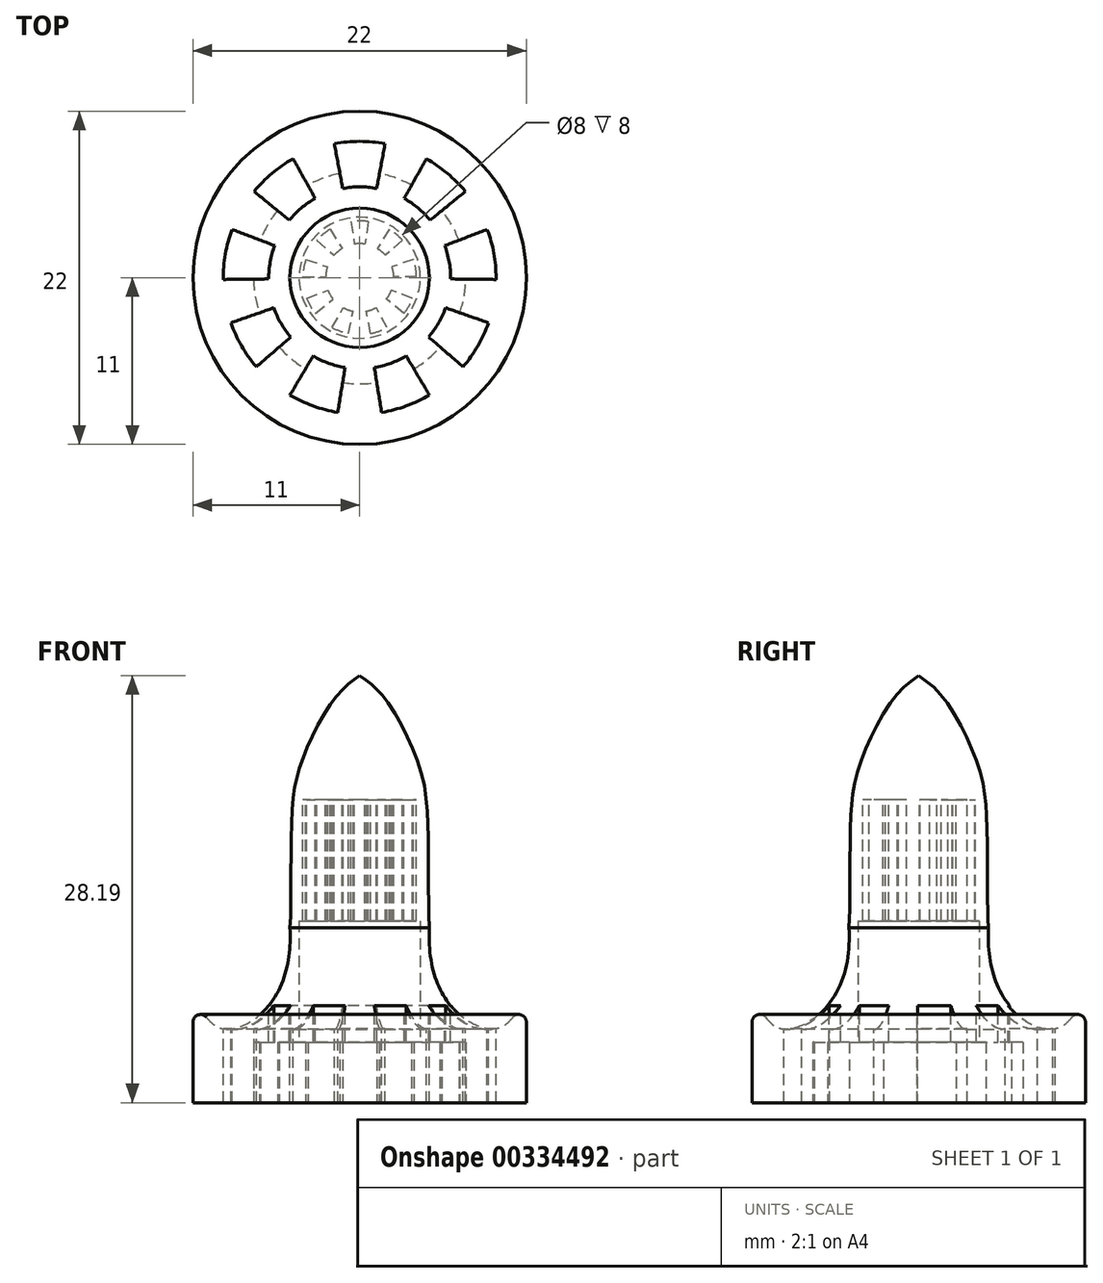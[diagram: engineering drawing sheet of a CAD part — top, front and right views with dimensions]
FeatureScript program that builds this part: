
annotation { "Feature Type Name" : "Feature", "Feature Type Description" : "" }
export const myFeature = defineFeature(function(context is Context, id is Id, definition is map)
    precondition{}
    {
        {
            var Q0;
            Q0=qCreatedBy(makeId("Top.planeOp"),FACE);
            var sketch = newSketch(context, id + "F0", { "sketchPlane" : qUnion([Q0])});
            skCircle(sketch, "E0", {"center": v(0, 0) * mm, "radius": 11 * mm});
            skSolve(sketch);
        }
        {
            var Q0;
            Q0=qSketchRegion(id+"F0",true);
            extrude(context, id + "F1", {"entities" : qUnion([Q0]), "depth" : 2 * mm});
        }
        {
            var Q0;
            Q0=qCreatedBy(makeId("Front.planeOp"),FACE);
            var sketch = newSketch(context, id + "F2", { "sketchPlane" : qUnion([Q0])});
            skPoint(sketch, "E1", {"position": v(0, 21.19) * mm});
            skLineSegment(sketch, "E2", {"start": v(0, 21.19) * mm, "end": v(0, 2) * mm});
            skLineSegment(sketch, "E3", {"start": v(-11, 2) * mm, "end": v(0, 2) * mm});
            skLineSegment(sketch, "E4", {"start": v(-11, 2) * mm, "end": v(-11, 7.23) * mm});
            skFitSpline(sketch, "E5", {"points": [v(-11, 7.23) * mm, v(-9.2, 4.92) * mm, v(-6.25, 6.13) * mm, v(-4.6, 11.53) * mm], "startDerivative": vector(4.68, -10.12) * mm, "endDerivative": vector(-0.82, 17.56) * mm});
            skLineSegment(sketch, "E6", {"start": v(0, 21.19) * mm, "end": v(0, 28.19) * mm});
            skFitSpline(sketch, "E7", {"points": [v(0, 28.19) * mm, v(-1.53, 26.84) * mm, v(-3.73, 22.78) * mm, v(-4.47, 18.95) * mm, v(-4.6, 11.53) * mm], "startDerivative": vector(-7.87, -5.55) * mm, "endDerivative": vector(-1, -14.63) * mm});
            skSolve(sketch);
        }
        {
            var Q0;
            Q0=qSketchRegion(id+"F2",true);
            var Q1;
            Q1=sQuery(id+"F2.wireOp",EDGE,"E2");
            revolve(context, id + "F3", {"operationType" : NewBodyOperationType.ADD, "entities" : qUnion([Q0]), "axis" : qUnion([Q1]), "revolveType" : RevolveType.FULL});
        }
        {
            var Q0;
            Q0=makeQuery(id+"F1.opExtrude","CAP_FACE",FACE,{"disambiguationData":[OSD([sQuery(id+"F0.wireOp",EDGE,"E0")])],"isStart":true});
            var sketch = newSketch(context, id + "F4", { "sketchPlane" : qUnion([Q0])});
            skCircle(sketch, "E8", {"center": v(0, 0) * mm, "radius": 7 * mm});
            skSolve(sketch);
        }
        {
            var Q0;
            Q0=qSketchRegion(id+"F4",true);
            extrude(context, id + "F5", {"entities" : qUnion([Q0]), "operationType" : NewBodyOperationType.REMOVE, "oppositeDirection" : true, "depth" : 4 * mm});
        }
        {
            var Q0;
            Q0=makeQuery(id+"F5.boolean.opBoolean","COPY",FACE,{"derivedFrom":makeQuery(id+"F5.opExtrude","CAP_FACE",FACE,{"disambiguationData":[OSD([sQuery(id+"F4.wireOp",EDGE,"E8")])],"isStart":false})});
            var sketch = newSketch(context, id + "F6", { "sketchPlane" : qUnion([Q0])});
            skCircle(sketch, "E9", {"center": v(0, 0) * mm, "radius": 4 * mm});
            skSolve(sketch);
        }
        {
            var Q0;
            Q0=qSketchRegion(id+"F6",true);
            extrude(context, id + "F7", {"entities" : qUnion([Q0]), "operationType" : NewBodyOperationType.REMOVE, "oppositeDirection" : true, "depth" : 8 * mm});
        }
        {
            var Q0;
            Q0=qCreatedBy(makeId("Top.planeOp"),FACE);
            cPlane(context, id + "F8", {"entities" : qUnion([Q0]), "cplaneType" : CPlaneType.OFFSET, "offset" : 20 * mm, "width" : 150 * mm, "height" : 150 * mm});
        }
        {
            var Q0;
            Q0=qCreatedBy(id+"F8.planeOp",FACE);
            var sketch = newSketch(context, id + "F9", { "sketchPlane" : qUnion([Q0])});
            skArc(sketch, "E10", {"start": v(1.12, 5.9) * mm, "mid": v(0, 6) * mm, "end": v(-1.12, 5.9) * mm});
            skArc(sketch, "E11", {"start": v(1.68, 8.84) * mm, "mid": v(0, 9) * mm, "end": v(-1.68, 8.84) * mm});
            skLineSegment(sketch, "E12", {"start": v(1.12, 5.9) * mm, "end": v(1.68, 8.84) * mm});
            skLineSegment(sketch, "E13.MirrorCS", {"start": v(-1.12, 5.9) * mm, "end": v(-1.68, 8.84) * mm});
            skLineSegment(sketch, "E14.1.0", {"start": v(-2.93, 5.23) * mm, "end": v(-4.4, 7.85) * mm});
            skArc(sketch, "E14.1.1", {"start": v(-4.4, 7.85) * mm, "mid": v(-5.79, 6.9) * mm, "end": v(-6.97, 5.7) * mm});
            skLineSegment(sketch, "E14.1.2", {"start": v(-4.65, 3.8) * mm, "end": v(-6.97, 5.7) * mm});
            skArc(sketch, "E14.1.3", {"start": v(-2.93, 5.23) * mm, "mid": v(-3.86, 4.6) * mm, "end": v(-4.65, 3.8) * mm});
            skLineSegment(sketch, "E14.2.0", {"start": v(-5.61, 2.12) * mm, "end": v(-8.42, 3.19) * mm});
            skArc(sketch, "E14.2.1", {"start": v(-8.42, 3.19) * mm, "mid": v(-8.86, 1.56) * mm, "end": v(-9, -0.11) * mm});
            skLineSegment(sketch, "E14.2.2", {"start": v(-6, -0.08) * mm, "end": v(-9, -0.11) * mm});
            skArc(sketch, "E14.2.3", {"start": v(-5.61, 2.12) * mm, "mid": v(-5.9, 1.04) * mm, "end": v(-6, -0.08) * mm});
            skLineSegment(sketch, "E14.3.0", {"start": v(-5.66, -1.98) * mm, "end": v(-8.5, -2.97) * mm});
            skArc(sketch, "E14.3.1", {"start": v(-8.5, -2.97) * mm, "mid": v(-7.8, -4.5) * mm, "end": v(-6.82, -5.87) * mm});
            skLineSegment(sketch, "E14.3.2", {"start": v(-4.55, -3.92) * mm, "end": v(-6.82, -5.87) * mm});
            skArc(sketch, "E14.3.3", {"start": v(-5.66, -1.98) * mm, "mid": v(-5.2, -3) * mm, "end": v(-4.55, -3.92) * mm});
            skLineSegment(sketch, "E14.4.0", {"start": v(-3.07, -5.16) * mm, "end": v(-4.6, -7.74) * mm});
            skArc(sketch, "E14.4.1", {"start": v(-4.6, -7.74) * mm, "mid": v(-3.08, -8.46) * mm, "end": v(-1.45, -8.88) * mm});
            skLineSegment(sketch, "E14.4.2", {"start": v(-0.97, -5.92) * mm, "end": v(-1.45, -8.88) * mm});
            skArc(sketch, "E14.4.3", {"start": v(-3.07, -5.16) * mm, "mid": v(-2.05, -5.64) * mm, "end": v(-0.97, -5.92) * mm});
            skLineSegment(sketch, "E14.5.0", {"start": v(0.97, -5.92) * mm, "end": v(1.45, -8.88) * mm});
            skArc(sketch, "E14.5.1", {"start": v(1.45, -8.88) * mm, "mid": v(3.08, -8.46) * mm, "end": v(4.6, -7.74) * mm});
            skLineSegment(sketch, "E14.5.2", {"start": v(3.07, -5.16) * mm, "end": v(4.6, -7.74) * mm});
            skArc(sketch, "E14.5.3", {"start": v(0.97, -5.92) * mm, "mid": v(2.05, -5.64) * mm, "end": v(3.07, -5.16) * mm});
            skLineSegment(sketch, "E14.6.0", {"start": v(4.55, -3.92) * mm, "end": v(6.82, -5.87) * mm});
            skArc(sketch, "E14.6.1", {"start": v(6.82, -5.87) * mm, "mid": v(7.8, -4.5) * mm, "end": v(8.5, -2.97) * mm});
            skLineSegment(sketch, "E14.6.2", {"start": v(5.66, -1.98) * mm, "end": v(8.5, -2.97) * mm});
            skArc(sketch, "E14.6.3", {"start": v(4.55, -3.92) * mm, "mid": v(5.2, -3) * mm, "end": v(5.66, -1.98) * mm});
            skLineSegment(sketch, "E14.7.0", {"start": v(6, -0.08) * mm, "end": v(9, -0.11) * mm});
            skArc(sketch, "E14.7.1", {"start": v(9, -0.11) * mm, "mid": v(8.86, 1.56) * mm, "end": v(8.42, 3.19) * mm});
            skLineSegment(sketch, "E14.7.2", {"start": v(5.61, 2.12) * mm, "end": v(8.42, 3.19) * mm});
            skArc(sketch, "E14.7.3", {"start": v(6, -0.08) * mm, "mid": v(5.9, 1.04) * mm, "end": v(5.61, 2.12) * mm});
            skLineSegment(sketch, "E14.8.0", {"start": v(4.65, 3.8) * mm, "end": v(6.97, 5.7) * mm});
            skArc(sketch, "E14.8.1", {"start": v(6.97, 5.7) * mm, "mid": v(5.79, 6.9) * mm, "end": v(4.4, 7.85) * mm});
            skLineSegment(sketch, "E14.8.2", {"start": v(2.93, 5.23) * mm, "end": v(4.4, 7.85) * mm});
            skArc(sketch, "E14.8.3", {"start": v(4.65, 3.8) * mm, "mid": v(3.86, 4.6) * mm, "end": v(2.93, 5.23) * mm});
            skSolve(sketch);
        }
        {
            var Q0;
            Q0=qSketchRegion(id+"F9",true);
            extrude(context, id + "F10", {"entities" : qUnion([Q0]), "operationType" : NewBodyOperationType.REMOVE, "oppositeDirection" : true, "depth" : 25 * mm});
        }
        {
            var Q0;
            Q0=qCreatedBy(id+"F8.planeOp",FACE);
            var sketch = newSketch(context, id + "F11", { "sketchPlane" : qUnion([Q0])});
            skArc(sketch, "E15", {"start": v(0.34, 2.22) * mm, "mid": v(0, 2.25) * mm, "end": v(-0.34, 2.22) * mm});
            skArc(sketch, "E16", {"start": v(0.57, 3.7) * mm, "mid": v(0, 3.75) * mm, "end": v(-0.57, 3.7) * mm});
            skLineSegment(sketch, "E17", {"start": v(0.34, 2.22) * mm, "end": v(0.57, 3.7) * mm});
            skLineSegment(sketch, "E18.MirrorCS", {"start": v(-0.34, 2.22) * mm, "end": v(-0.57, 3.7) * mm});
            skLineSegment(sketch, "E19.1.0", {"start": v(-1.7, 1.48) * mm, "end": v(-2.82, 2.47) * mm});
            skArc(sketch, "E19.1.1", {"start": v(-1.94, 3.2) * mm, "mid": v(-2.41, 2.87) * mm, "end": v(-2.82, 2.47) * mm});
            skLineSegment(sketch, "E19.1.2", {"start": v(-1.17, 1.92) * mm, "end": v(-1.94, 3.2) * mm});
            skArc(sketch, "E19.1.3", {"start": v(-1.17, 1.92) * mm, "mid": v(-1.45, 1.72) * mm, "end": v(-1.7, 1.48) * mm});
            skLineSegment(sketch, "E19.2.0", {"start": v(-2.25, 0.05) * mm, "end": v(-3.75, 0.08) * mm});
            skArc(sketch, "E19.2.1", {"start": v(-3.55, 1.2) * mm, "mid": v(-3.7, 0.65) * mm, "end": v(-3.75, 0.08) * mm});
            skLineSegment(sketch, "E19.2.2", {"start": v(-2.13, 0.73) * mm, "end": v(-3.55, 1.2) * mm});
            skArc(sketch, "E19.2.3", {"start": v(-2.13, 0.73) * mm, "mid": v(-2.22, 0.4) * mm, "end": v(-2.25, 0.05) * mm});
            skLineSegment(sketch, "E19.3.0", {"start": v(-1.75, -1.41) * mm, "end": v(-2.92, -2.35) * mm});
            skArc(sketch, "E19.3.1", {"start": v(-3.5, -1.36) * mm, "mid": v(-3.25, -1.87) * mm, "end": v(-2.92, -2.35) * mm});
            skLineSegment(sketch, "E19.3.2", {"start": v(-2.1, -0.81) * mm, "end": v(-3.5, -1.36) * mm});
            skArc(sketch, "E19.3.3", {"start": v(-2.1, -0.81) * mm, "mid": v(-1.95, -1.12) * mm, "end": v(-1.75, -1.41) * mm});
            skLineSegment(sketch, "E19.4.0", {"start": v(-0.44, -2.2) * mm, "end": v(-0.73, -3.68) * mm});
            skArc(sketch, "E19.4.1", {"start": v(-1.8, -3.29) * mm, "mid": v(-1.28, -3.52) * mm, "end": v(-0.73, -3.68) * mm});
            skLineSegment(sketch, "E19.4.2", {"start": v(-1.08, -1.97) * mm, "end": v(-1.8, -3.29) * mm});
            skArc(sketch, "E19.4.3", {"start": v(-1.08, -1.97) * mm, "mid": v(-0.77, -2.11) * mm, "end": v(-0.44, -2.2) * mm});
            skLineSegment(sketch, "E19.5.0", {"start": v(1.08, -1.97) * mm, "end": v(1.8, -3.29) * mm});
            skArc(sketch, "E19.5.1", {"start": v(0.73, -3.68) * mm, "mid": v(1.28, -3.52) * mm, "end": v(1.8, -3.29) * mm});
            skLineSegment(sketch, "E19.5.2", {"start": v(0.44, -2.2) * mm, "end": v(0.73, -3.68) * mm});
            skArc(sketch, "E19.5.3", {"start": v(0.44, -2.2) * mm, "mid": v(0.77, -2.11) * mm, "end": v(1.08, -1.97) * mm});
            skLineSegment(sketch, "E19.6.0", {"start": v(2.1, -0.81) * mm, "end": v(3.5, -1.36) * mm});
            skArc(sketch, "E19.6.1", {"start": v(2.92, -2.35) * mm, "mid": v(3.25, -1.88) * mm, "end": v(3.5, -1.36) * mm});
            skLineSegment(sketch, "E19.6.2", {"start": v(1.75, -1.41) * mm, "end": v(2.92, -2.35) * mm});
            skArc(sketch, "E19.6.3", {"start": v(1.75, -1.41) * mm, "mid": v(1.95, -1.13) * mm, "end": v(2.1, -0.81) * mm});
            skLineSegment(sketch, "E19.7.0", {"start": v(2.13, 0.73) * mm, "end": v(3.55, 1.2) * mm});
            skArc(sketch, "E19.7.1", {"start": v(3.75, 0.08) * mm, "mid": v(3.7, 0.65) * mm, "end": v(3.55, 1.2) * mm});
            skLineSegment(sketch, "E19.7.2", {"start": v(2.25, 0.05) * mm, "end": v(3.75, 0.08) * mm});
            skArc(sketch, "E19.7.3", {"start": v(2.25, 0.05) * mm, "mid": v(2.22, 0.4) * mm, "end": v(2.13, 0.73) * mm});
            skLineSegment(sketch, "E19.8.0", {"start": v(1.17, 1.92) * mm, "end": v(1.94, 3.2) * mm});
            skArc(sketch, "E19.8.1", {"start": v(2.82, 2.47) * mm, "mid": v(2.41, 2.87) * mm, "end": v(1.94, 3.2) * mm});
            skLineSegment(sketch, "E19.8.2", {"start": v(1.7, 1.48) * mm, "end": v(2.82, 2.47) * mm});
            skArc(sketch, "E19.8.3", {"start": v(1.7, 1.48) * mm, "mid": v(1.45, 1.72) * mm, "end": v(1.17, 1.92) * mm});
            skSolve(sketch);
        }
        {
            var Q0;
            Q0=qSketchRegion(id+"F11",true);
            extrude(context, id + "F12", {"entities" : qUnion([Q0]), "operationType" : NewBodyOperationType.REMOVE, "oppositeDirection" : true, "depth" : 25 * mm});
        }
        {
            var Q0;
            Q0=makeQuery(id+"F3.opRevolve","SWEPT_EDGE",EDGE,{"disambiguationData":[OSD([sQuery(id+"F2.wireOp",EDGE,"E4"),sQuery(id+"F2.wireOp",EDGE,"E5")])]});
            fillet(context, id + "F13", {"entities" : qUnion([Q0]), "radius" : .5 * mm, "tangentPropagation" : true, "allowEdgeOverflow" : false});
        }
    });
